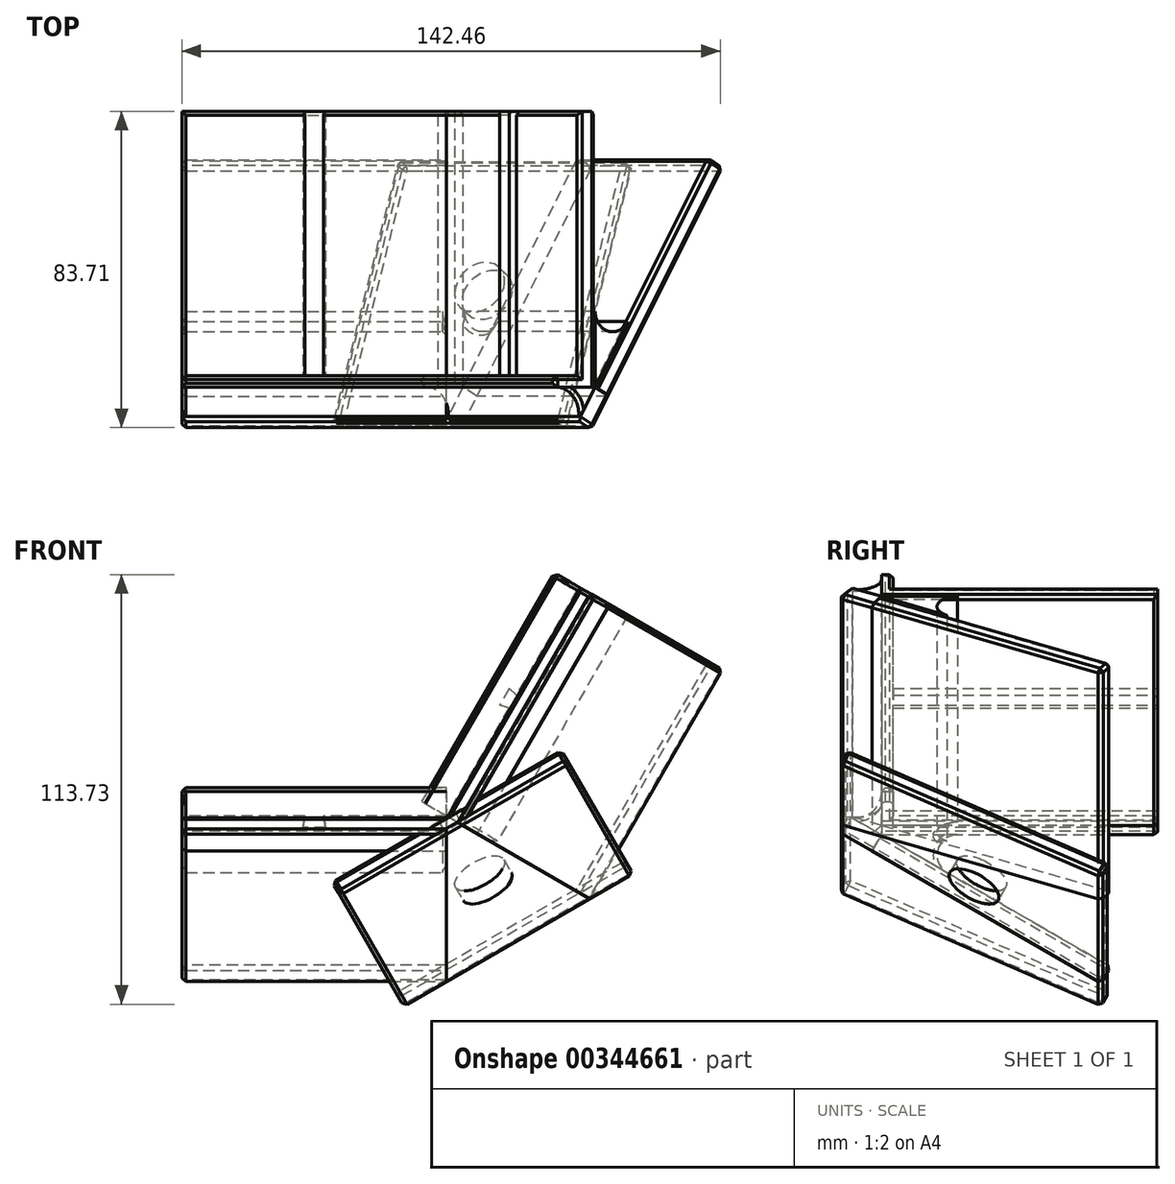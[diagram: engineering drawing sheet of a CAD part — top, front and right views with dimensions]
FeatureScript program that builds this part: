
annotation { "Feature Type Name" : "Feature", "Feature Type Description" : "" }
export const myFeature = defineFeature(function(context is Context, id is Id, definition is map)
    precondition{}
    {
        {
            var Q0;
            Q0=qCreatedBy(makeId("Top.planeOp"),FACE);
            var sketch = newSketch(context, id + "F0", { "sketchPlane" : qUnion([Q0])});
            skLineSegment(sketch, "E0.bottom", {"start": v(35, 35) * mm, "end": v(-35, 35) * mm});
            skLineSegment(sketch, "E0.top", {"start": v(35, -35) * mm, "end": v(-35, -35) * mm});
            skLineSegment(sketch, "E0.left", {"start": v(35, 35) * mm, "end": v(35, -35) * mm});
            skLineSegment(sketch, "E0.right", {"start": v(-35, 35) * mm, "end": v(-35, -35) * mm});
            skPoint(sketch, "E0.middle", {"position": v(0, 0) * mm});
            skSolve(sketch);
        }
        {
            var Q0;
            Q0=makeQuery(id+"F0.imprint","IMPRINT",FACE,{"disambiguationData":[TD([[makeQuery(id+"F0.imprint","IMPRINT",EDGE,{"derivedFrom":sQuery(id+"F0.wireOp",EDGE,"E0.bottom")}),1.0]])]});
            extrude(context, id + "F1", {"entities" : qUnion([Q0]), "depth" : 5 * mm});
        }
        {
            var Q0;
            Q0=makeQuery(id+"F1.opExtrude","SWEPT_FACE",FACE,{"disambiguationData":[OSD([sQuery(id+"F0.wireOp",EDGE,"E0.top")])]});
            var sketch = newSketch(context, id + "F2", { "sketchPlane" : qUnion([Q0])});
            skLineSegment(sketch, "E1", {"start": v(0, 5) * mm, "end": v(2.5, 5) * mm});
            skLineSegment(sketch, "E2", {"start": v(0, 2) * mm, "end": v(3, 2) * mm});
            skLineSegment(sketch, "E3", {"start": v(3, 2) * mm, "end": v(2.5, 5) * mm});
            skLineSegment(sketch, "E4", {"start": v(0, 2) * mm, "end": v(-3, 2) * mm});
            skLineSegment(sketch, "E5", {"start": v(0, 5) * mm, "end": v(-2.5, 5) * mm});
            skLineSegment(sketch, "E6", {"start": v(-2.5, 5) * mm, "end": v(-3, 2) * mm});
            skSolve(sketch);
        }
        {
            var Q0;
            Q0=makeQuery(id+"F1.opExtrude","SWEPT_FACE",FACE,{"disambiguationData":[OSD([sQuery(id+"F0.wireOp",EDGE,"E0.top")])]});
            var sketch = newSketch(context, id + "F3", { "sketchPlane" : qUnion([Q0])});
            skLineSegment(sketch, "E7.bottom", {"start": v(-35, 0) * mm, "end": v(35, 0) * mm});
            skLineSegment(sketch, "E7.top", {"start": v(-35, 12.5) * mm, "end": v(35, 12.5) * mm});
            skLineSegment(sketch, "E7.left", {"start": v(-35, 0) * mm, "end": v(-35, 12.5) * mm});
            skLineSegment(sketch, "E7.right", {"start": v(35, 0) * mm, "end": v(35, 12.5) * mm});
            skSolve(sketch);
        }
        {
            var Q0;
            Q0=qSketchRegion(id+"F3",true);
            extrude(context, id + "F4", {"entities" : qUnion([Q0]), "operationType" : NewBodyOperationType.ADD, "depth" : 3 * mm});
        }
        {
            var Q0;
            Q0=makeQuery(id+"F4.opExtrude","CAP_EDGE",EDGE,{"disambiguationData":[OSD([sQuery(id+"F3.wireOp",EDGE,"E7.bottom")])],"isStart":false});
            var Q1;
            Q1=makeQuery(id+"F4.boolean.opBoolean","MERGE",EDGE,{"derivedFrom":[makeQuery(id+"F1.opExtrude","CAP_EDGE",EDGE,{"disambiguationData":[OSD([sQuery(id+"F0.wireOp",EDGE,"E0.left")])],"isStart":true}),makeQuery(id+"F4.opExtrude","SWEPT_EDGE",EDGE,{"disambiguationData":[OSD([sQuery(id+"F3.wireOp",EDGE,"E7.bottom"),sQuery(id+"F3.wireOp",EDGE,"E7.right")])]})]});
            cPlane(context, id + "F5", {"entities" : qUnion([Q0, Q1]), "cplaneType" : CPlaneType.LINE_ANGLE, "offset" : 25 * mm, "angle" : 30 * degree, "width" : 150 * mm, "height" : 150 * mm});
        }
        {
            var Q0;
            Q0=qCreatedBy(id+"F5.planeOp",FACE);
            var sketch = newSketch(context, id + "F6", { "sketchPlane" : qUnion([Q0])});
            skLineSegment(sketch, "E8.bottom", {"start": v(-35, -32.9) * mm, "end": v(35, -32.9) * mm});
            skLineSegment(sketch, "E8.top", {"start": v(-35, 37.1) * mm, "end": v(35, 37.1) * mm});
            skLineSegment(sketch, "E8.left", {"start": v(-35, -32.9) * mm, "end": v(-35, 37.1) * mm});
            skLineSegment(sketch, "E8.right", {"start": v(35, -32.9) * mm, "end": v(35, 37.1) * mm});
            skSolve(sketch);
        }
        {
            var Q0;
            Q0=qSketchRegion(id+"F6",true);
            extrude(context, id + "F7", {"entities" : qUnion([Q0]), "operationType" : NewBodyOperationType.ADD, "oppositeDirection" : true, "depth" : 5 * mm});
        }
        {
            var Q0;
            Q0=makeQuery(id+"F7.opExtrude","SWEPT_FACE",FACE,{"disambiguationData":[OSD([sQuery(id+"F6.wireOp",EDGE,"E8.bottom")])]});
            extrude(context, id + "F8", {"entities" : qUnion([Q0]), "depth" : 10 * mm});
        }
        {
            var Q0;
            Q0=makeQuery(id+"F7.opExtrude","SWEPT_FACE",FACE,{"disambiguationData":[OSD([sQuery(id+"F6.wireOp",EDGE,"E8.right")])]});
            var sketch = newSketch(context, id + "F9", { "sketchPlane" : qUnion([Q0])});
            skLineSegment(sketch, "E9", {"start": v(-38, 0) * mm, "end": v(-20.68, -10) * mm});
            skLineSegment(sketch, "E10", {"start": v(-18, 0) * mm, "end": v(-38, 0) * mm});
            skLineSegment(sketch, "E11", {"start": v(-38, 0) * mm, "end": v(-45.8, 4.5) * mm});
            skLineSegment(sketch, "E12", {"start": v(-38, 0) * mm, "end": v(-38, 11.5) * mm});
            skArc(sketch, "E13", {"start": v(-45.8, 4.5) * mm, "mid": v(-40.34, 6.26) * mm, "end": v(-38, 11.5) * mm});
            skArc(sketch, "E14", {"start": v(-18, 0) * mm, "mid": v(-23.18, -3.97) * mm, "end": v(-20.68, -10) * mm});
            skSolve(sketch);
        }
        {
            var Q0;
            Q0=qSketchRegion(id+"F9",true);
            var Q1;
            Q1=makeQuery(id+"F7.opExtrude","SWEPT_FACE",FACE,{"disambiguationData":[OSD([sQuery(id+"F6.wireOp",EDGE,"E8.left")])]});
            extrude(context, id + "F10", {"entities" : qUnion([Q0]), "endBound" : BoundingType.UP_TO_SURFACE, "oppositeDirection" : true, "endBoundEntityFace" : qUnion([Q1]), "depth" : 25 * mm});
        }
        {
            var Q0;
            {var subQ0=sQuery(id+"F0.wireOp",EDGE,"E0.bottom");var subQ1=sQuery(id+"F0.wireOp",EDGE,"E0.top");var subQ2=sQuery(id+"F0.wireOp",EDGE,"E0.left");Q0=makeQuery(id+"F13.boolean.opBoolean","SPLIT",FACE,{"disambiguationData":[TD([makeQuery(id+"F1.opExtrude","SWEPT_FACE",FACE,{"disambiguationData":[OSD([subQ2])]})])],"derivedFrom":makeQuery(id+"F1.opExtrude","CAP_FACE",FACE,{"disambiguationData":[OSD([subQ0,subQ1,subQ2,sQuery(id+"F0.wireOp",EDGE,"E0.right")])],"isStart":false})});}
            var Q1;
            Q1=makeQuery(id+"F1.opExtrude","CAP_EDGE",EDGE,{"disambiguationData":[OSD([sQuery(id+"F0.wireOp",EDGE,"E0.left")])],"isStart":false});
            cPlane(context, id + "F11", {"entities" : qUnion([Q0, Q1]), "cplaneType" : CPlaneType.LINE_ANGLE, "offset" : 25 * mm, "angle" : 60 * degree, "oppositeDirection" : true, "width" : 150 * mm, "height" : 150 * mm});
        }
        {
            var Q0;
            Q0=makeQuery(id+"F1.opExtrude","SWEPT_BODY",BODY,{"disambiguationData":[OSD([sQuery(id+"F0.wireOp",EDGE,"E0.bottom"),sQuery(id+"F0.wireOp",EDGE,"E0.top"),sQuery(id+"F0.wireOp",EDGE,"E0.left"),sQuery(id+"F0.wireOp",EDGE,"E0.right")])]});
            var Q1;
            Q1=makeQuery(id+"F7.opExtrude","SWEPT_BODY",BODY,{"disambiguationData":[OSD([sQuery(id+"F6.wireOp",EDGE,"E8.bottom"),sQuery(id+"F6.wireOp",EDGE,"E8.top"),sQuery(id+"F6.wireOp",EDGE,"E8.left"),sQuery(id+"F6.wireOp",EDGE,"E8.right")])]});
            var Q2;
            Q2=makeQuery(id+"F8.opExtrude","SWEPT_BODY",BODY,{"disambiguationData":[OSD([sQuery(id+"F6.wireOp",EDGE,"E8.bottom")])]});
            var Q3;
            Q3=makeQuery(id+"F10.opExtrude","SWEPT_BODY",BODY,{"disambiguationData":[OSD([sQuery(id+"F9.wireOp",EDGE,"E9"),sQuery(id+"F9.wireOp",EDGE,"E10"),sQuery(id+"F9.wireOp",EDGE,"E14")])]});
            var Q4;
            Q4=makeQuery(id+"F10.opExtrude","SWEPT_BODY",BODY,{"disambiguationData":[OSD([sQuery(id+"F9.wireOp",EDGE,"E11"),sQuery(id+"F9.wireOp",EDGE,"E12"),sQuery(id+"F9.wireOp",EDGE,"E13")])]});
            var Q5;
            Q5=qCreatedBy(id+"F11.planeOp",FACE);
            mirror(context, id + "F12", {"entities" : qUnion([Q0, Q1, Q2, Q3, Q4]), "mirrorPlane" : qUnion([Q5])});
        }
        {
            var Q0;
            Q0=makeQuery(id+"F2.imprint","IMPRINT",FACE,{"disambiguationData":[TD([[makeQuery(id+"F2.imprint","IMPRINT",EDGE,{"derivedFrom":sQuery(id+"F2.wireOp",EDGE,"E1")}),1.0]])]});
            var Q1;
            Q1=makeQuery(id+"F1.opExtrude","SWEPT_FACE",FACE,{"disambiguationData":[OSD([sQuery(id+"F0.wireOp",EDGE,"E0.bottom")])]});
            extrude(context, id + "F13", {"entities" : qUnion([Q0]), "operationType" : NewBodyOperationType.REMOVE, "endBound" : BoundingType.UP_TO_SURFACE, "oppositeDirection" : true, "endBoundEntityFace" : qUnion([Q1]), "depth" : 25 * mm});
        }
        {
            var Q0;
            Q0=makeQuery(id+"F7.opExtrude","CAP_VERTEX",VERTEX,{"disambiguationData":[OSD([sQuery(id+"F6.wireOp",EDGE,"E8.top"),sQuery(id+"F6.wireOp",EDGE,"E8.right")])],"isStart":false});
            var Q1;
            Q1=makeQuery(id+"F12.opPattern","COPY",VERTEX,{"derivedFrom":makeQuery(id+"F7.opExtrude","CAP_VERTEX",VERTEX,{"disambiguationData":[OSD([sQuery(id+"F6.wireOp",EDGE,"E8.top"),sQuery(id+"F6.wireOp",EDGE,"E8.right")])],"isStart":false}),"instanceName":"1"});
            var Q2;
            Q2=makeQuery(id+"F12.opPattern","COPY",VERTEX,{"derivedFrom":makeQuery(id+"F7.opExtrude","CAP_VERTEX",VERTEX,{"disambiguationData":[OSD([sQuery(id+"F6.wireOp",EDGE,"E8.bottom"),sQuery(id+"F6.wireOp",EDGE,"E8.right")])],"isStart":false}),"instanceName":"1"});
            cPlane(context, id + "F14", {"entities" : qUnion([Q0, Q1, Q2]), "cplaneType" : CPlaneType.THREE_POINT, "offset" : 25 * mm, "width" : 150 * mm, "height" : 150 * mm});
        }
        {
            var Q0;
            Q0=qCreatedBy(id+"F14.planeOp",FACE);
            var sketch = newSketch(context, id + "F15", { "sketchPlane" : qUnion([Q0])});
            skLineSegment(sketch, "E15", {"start": v(20.57, 37.1) * mm, "end": v(63.5, 26) * mm, "construction": true});
            skLineSegment(sketch, "E16", {"start": v(20.57, -42.9) * mm, "end": v(24.76, -44) * mm, "construction": true});
            skLineSegment(sketch, "E17", {"start": v(22.67, -43.45) * mm, "end": v(42.03, 31.55) * mm, "construction": true});
            skLineSegment(sketch, "E18", {"start": v(42.03, 31.55) * mm, "end": v(8.14, 40.3) * mm});
            skLineSegment(sketch, "E19", {"start": v(42.03, 31.55) * mm, "end": v(75.92, 22.8) * mm});
            skLineSegment(sketch, "E20", {"start": v(22.67, -43.45) * mm, "end": v(-11.22, -34.7) * mm});
            skLineSegment(sketch, "E21", {"start": v(22.67, -43.45) * mm, "end": v(56.56, -52.2) * mm});
            skLineSegment(sketch, "E22", {"start": v(56.56, -52.2) * mm, "end": v(75.92, 22.8) * mm});
            skLineSegment(sketch, "E23", {"start": v(8.14, 40.3) * mm, "end": v(-11.22, -34.7) * mm});
            skSolve(sketch);
        }
        {
            var Q0;
            Q0=makeQuery(id+"F15.imprint","IMPRINT",FACE,{"disambiguationData":[TD([[makeQuery(id+"F15.imprint","IMPRINT",EDGE,{"derivedFrom":sQuery(id+"F15.wireOp",EDGE,"E18")}),1.0]])]});
            var Q1;
            Q1=makeQuery(id+"F10.opExtrude","CAP_VERTEX",VERTEX,{"disambiguationData":[OSD([sQuery(id+"F6.wireOp",EDGE,"E8.right"),sQuery(id+"F9.wireOp",EDGE,"E9"),sQuery(id+"F9.wireOp",EDGE,"E14")])],"isStart":true});
            extrude(context, id + "F16", {"entities" : qUnion([Q0]), "endBound" : BoundingType.UP_TO_VERTEX, "endBoundEntityVertex" : qUnion([Q1]), "depth" : 25 * mm});
        }
        {
            var Q0;
            Q0=makeQuery(id+"F4.boolean.opBoolean","MERGE",EDGE,{"derivedFrom":[makeQuery(id+"F1.opExtrude","CAP_EDGE",EDGE,{"disambiguationData":[OSD([sQuery(id+"F0.wireOp",EDGE,"E0.left")])],"isStart":true}),makeQuery(id+"F4.opExtrude","SWEPT_EDGE",EDGE,{"disambiguationData":[OSD([sQuery(id+"F3.wireOp",EDGE,"E7.bottom"),sQuery(id+"F3.wireOp",EDGE,"E7.right")])]})]});
            cPoint(context, id + "F17", {"entities" : qUnion([Q0]), "parameter" : 0.5});
        }
        {
            var Q0;
            Q0=makeQuery(id+"F1.opExtrude","CAP_VERTEX",VERTEX,{"disambiguationData":[OSD([sQuery(id+"F0.wireOp",EDGE,"E0.bottom"),sQuery(id+"F0.wireOp",EDGE,"E0.left")])],"isStart":true});
            var Q1;
            Q1 = qCreatedBy(id + "F17" ,VERTEX);
            var Q2;
            Q2=makeQuery(id+"F12.opPattern","COPY",VERTEX,{"derivedFrom":makeQuery(id+"F1.opExtrude","CAP_VERTEX",VERTEX,{"disambiguationData":[OSD([sQuery(id+"F0.wireOp",EDGE,"E0.bottom"),sQuery(id+"F0.wireOp",EDGE,"E0.left")])],"isStart":true}),"instanceName":"1"});
            cPlane(context, id + "F18", {"entities" : qUnion([Q0, Q1, Q2]), "cplaneType" : CPlaneType.THREE_POINT, "offset" : 25 * mm, "width" : 150 * mm, "height" : 150 * mm});
        }
        {
            var Q0;
            Q0=qCreatedBy(id+"F18.planeOp",FACE);
            var sketch = newSketch(context, id + "F19", { "sketchPlane" : qUnion([Q0])});
            skLineSegment(sketch, "E24", {"start": v(35.31, -35) * mm, "end": v(35.31, 38) * mm});
            skLineSegment(sketch, "E25", {"start": v(35.31, 38) * mm, "end": v(30.31, 38) * mm});
            skLineSegment(sketch, "E26", {"start": v(30.31, 38) * mm, "end": v(30.31, -35) * mm});
            skLineSegment(sketch, "E27", {"start": v(30.31, -35) * mm, "end": v(35.31, -35) * mm});
            skSolve(sketch);
        }
        {
            var Q0;
            Q0 = qSketchRegion(id + "F19", true);
            var Q1;
            Q1=makeQuery(id+"F1.opExtrude","CAP_VERTEX",VERTEX,{"disambiguationData":[OSD([sQuery(id+"F0.wireOp",EDGE,"E0.top"),sQuery(id+"F0.wireOp",EDGE,"E0.left")])],"isStart":false});
            extrude(context, id + "F20", {"entities" : qUnion([Q0]), "endBound" : BoundingType.UP_TO_VERTEX, "oppositeDirection" : true, "endBoundEntityVertex" : qUnion([Q1]), "depth" : 25 * mm});
        }
        {
            var Q0;
            Q0=makeQuery(id+"F12.opPattern","COPY",FACE,{"derivedFrom":makeQuery(id+"F1.opExtrude","SWEPT_FACE",FACE,{"disambiguationData":[OSD([sQuery(id+"F0.wireOp",EDGE,"E0.bottom")])]}),"instanceName":"1"});
            var sketch = newSketch(context, id + "F21", { "sketchPlane" : qUnion([Q0])});
            skLineSegment(sketch, "E28", {"start": v(-53.5, 37.04) * mm, "end": v(-51.5, 33.58) * mm});
            skPoint(sketch, "E28.endSnap0", {"position": v(-57.27, 33.58) * mm});
            skLineSegment(sketch, "E29", {"start": v(-50.33, 36.56) * mm, "end": v(-49.08, 34.4) * mm});
            skLineSegment(sketch, "E30", {"start": v(-50.33, 36.56) * mm, "end": v(-51.58, 38.73) * mm});
            skLineSegment(sketch, "E31", {"start": v(-53.5, 37.04) * mm, "end": v(-51.58, 38.73) * mm});
            skLineSegment(sketch, "E32", {"start": v(-51.5, 33.58) * mm, "end": v(-49.08, 34.4) * mm});
            skSolve(sketch);
        }
        {
            var Q0;
            Q0 = qSketchRegion(id + "F21", true);
            var Q1;
            Q1=makeQuery(id+"F12.opPattern","COPY",FACE,{"derivedFrom":makeQuery(id+"F4.opExtrude","CAP_FACE",FACE,{"disambiguationData":[OSD([sQuery(id+"F3.wireOp",EDGE,"E7.bottom"),sQuery(id+"F3.wireOp",EDGE,"E7.top"),sQuery(id+"F3.wireOp",EDGE,"E7.left"),sQuery(id+"F3.wireOp",EDGE,"E7.right")])],"isStart":true}),"instanceName":"1"});
            extrude(context, id + "F22", {"entities" : qUnion([Q0]), "operationType" : NewBodyOperationType.ADD, "endBound" : BoundingType.UP_TO_SURFACE, "oppositeDirection" : true, "endBoundEntityFace" : qUnion([Q1]), "depth" : 25 * mm});
        }
        {
            var Q0;
            Q0=makeQuery(id+"F16.opExtrude","CAP_FACE",FACE,{"disambiguationData":[OSD([sQuery(id+"F15.wireOp",EDGE,"E18"),sQuery(id+"F15.wireOp",EDGE,"E19"),sQuery(id+"F15.wireOp",EDGE,"E20"),sQuery(id+"F15.wireOp",EDGE,"E21"),sQuery(id+"F15.wireOp",EDGE,"E22"),sQuery(id+"F15.wireOp",EDGE,"E23")])],"isStart":true});
            var sketch = newSketch(context, id + "F23", { "sketchPlane" : qUnion([Q0])});
            skLineSegment(sketch, "E33", {"start": v(66.24, 14.7) * mm, "end": v(-1.02, -4.82) * mm, "construction": true});
            skLineSegment(sketch, "E34", {"start": v(42.03, -31.55) * mm, "end": v(22.67, 43.45) * mm, "construction": true});
            skCircle(sketch, "E35", {"center": v(32.61, 4.94) * mm, "radius": 7.38 * mm});
            skSolve(sketch);
        }
        {
            var Q0;
            Q0=makeQuery(id+"F23.imprint","IMPRINT",FACE,{"disambiguationData":[TD([[makeQuery(id+"F23.imprint","IMPRINT",EDGE,{"derivedFrom":sQuery(id+"F23.wireOp",EDGE,"E35")}),1.0]])]});
            var Q1;
            Q1=makeQuery(id+"F16.opExtrude","CAP_FACE",FACE,{"disambiguationData":[OSD([sQuery(id+"F15.wireOp",EDGE,"E18"),sQuery(id+"F15.wireOp",EDGE,"E19"),sQuery(id+"F15.wireOp",EDGE,"E20"),sQuery(id+"F15.wireOp",EDGE,"E21"),sQuery(id+"F15.wireOp",EDGE,"E22"),sQuery(id+"F15.wireOp",EDGE,"E23")])],"isStart":false});
            extrude(context, id + "F24", {"entities" : qUnion([Q0]), "operationType" : NewBodyOperationType.REMOVE, "endBound" : BoundingType.UP_TO_SURFACE, "oppositeDirection" : true, "endBoundEntityFace" : qUnion([Q1]), "depth" : 25 * mm});
        }
        {
            var Q0;
            Q0=makeQuery(id+"F1.opExtrude","CAP_EDGE",EDGE,{"disambiguationData":[OSD([sQuery(id+"F0.wireOp",EDGE,"E0.right")])],"isStart":false});
            var Q1;
            {var subQ0=sQuery(id+"F0.wireOp",EDGE,"E0.right");var subQ1=sQuery(id+"F0.wireOp",EDGE,"E0.bottom");Q1=makeQuery(id+"F13.boolean.opBoolean","SPLIT",EDGE,{"disambiguationData":[TD([makeQuery(id+"F1.opExtrude","SWEPT_FACE",FACE,{"disambiguationData":[OSD([subQ0])]})])],"derivedFrom":makeQuery(id+"F1.opExtrude","CAP_EDGE",EDGE,{"disambiguationData":[OSD([subQ1])],"isStart":false})});}
            var Q2;
            {var subQ0=sQuery(id+"F0.wireOp",EDGE,"E0.left");var subQ1=sQuery(id+"F0.wireOp",EDGE,"E0.bottom");Q2=makeQuery(id+"F13.boolean.opBoolean","SPLIT",EDGE,{"disambiguationData":[TD([makeQuery(id+"F1.opExtrude","SWEPT_FACE",FACE,{"disambiguationData":[OSD([subQ0])]})])],"derivedFrom":makeQuery(id+"F1.opExtrude","CAP_EDGE",EDGE,{"disambiguationData":[OSD([subQ1])],"isStart":false})});}
            var Q3;
            Q3=makeQuery(id+"F12.opPattern","COPY",EDGE,{"derivedFrom":makeQuery(id+"F1.opExtrude","CAP_EDGE",EDGE,{"disambiguationData":[OSD([sQuery(id+"F0.wireOp",EDGE,"E0.bottom")])],"isStart":false}),"instanceName":"1"});
            var Q4;
            Q4=makeQuery(id+"F4.opExtrude","CAP_EDGE",EDGE,{"disambiguationData":[OSD([sQuery(id+"F3.wireOp",EDGE,"E7.left")])],"isStart":true});
            var Q5;
            Q5=makeQuery(id+"F4.opExtrude","CAP_EDGE",EDGE,{"disambiguationData":[OSD([sQuery(id+"F3.wireOp",EDGE,"E7.top")])],"isStart":true});
            var Q6;
            Q6=makeQuery(id+"F4.opExtrude","SWEPT_EDGE",EDGE,{"disambiguationData":[OSD([sQuery(id+"F3.wireOp",EDGE,"E7.top"),sQuery(id+"F3.wireOp",EDGE,"E7.left")])]});
            var Q7;
            Q7=makeQuery(id+"F4.opExtrude","CAP_EDGE",EDGE,{"disambiguationData":[OSD([sQuery(id+"F3.wireOp",EDGE,"E7.top")])],"isStart":false});
            var Q8;
            Q8=makeQuery(id+"F12.opPattern","COPY",EDGE,{"derivedFrom":makeQuery(id+"F4.opExtrude","CAP_EDGE",EDGE,{"disambiguationData":[OSD([sQuery(id+"F3.wireOp",EDGE,"E7.top")])],"isStart":true}),"instanceName":"1"});
            var Q9;
            Q9=makeQuery(id+"F12.opPattern","COPY",EDGE,{"derivedFrom":makeQuery(id+"F4.opExtrude","CAP_EDGE",EDGE,{"disambiguationData":[OSD([sQuery(id+"F3.wireOp",EDGE,"E7.top")])],"isStart":false}),"instanceName":"1"});
            var Q10;
            Q10=makeQuery(id+"F12.opPattern","COPY",EDGE,{"derivedFrom":makeQuery(id+"F4.opExtrude","SWEPT_EDGE",EDGE,{"disambiguationData":[OSD([sQuery(id+"F3.wireOp",EDGE,"E7.top"),sQuery(id+"F3.wireOp",EDGE,"E7.left")])]}),"instanceName":"1"});
            var Q11;
            Q11=makeQuery(id+"F12.opPattern","COPY",EDGE,{"derivedFrom":makeQuery(id+"F4.opExtrude","CAP_EDGE",EDGE,{"disambiguationData":[OSD([sQuery(id+"F3.wireOp",EDGE,"E7.left")])],"isStart":true}),"instanceName":"1"});
            var Q12;
            Q12=makeQuery(id+"F12.opPattern","COPY",EDGE,{"derivedFrom":makeQuery(id+"F1.opExtrude","CAP_EDGE",EDGE,{"disambiguationData":[OSD([sQuery(id+"F0.wireOp",EDGE,"E0.right")])],"isStart":false}),"instanceName":"1"});
            var Q13;
            Q13=makeQuery(id+"F12.opPattern","COPY",EDGE,{"derivedFrom":makeQuery(id+"F4.boolean.opBoolean","MERGE",EDGE,{"derivedFrom":[makeQuery(id+"F1.opExtrude","CAP_EDGE",EDGE,{"disambiguationData":[OSD([sQuery(id+"F0.wireOp",EDGE,"E0.right")])],"isStart":true}),makeQuery(id+"F4.opExtrude","SWEPT_EDGE",EDGE,{"disambiguationData":[OSD([sQuery(id+"F3.wireOp",EDGE,"E7.bottom"),sQuery(id+"F3.wireOp",EDGE,"E7.left")])]})]}),"instanceName":"1"});
            var Q14;
            Q14=makeQuery(id+"F12.opPattern","COPY",EDGE,{"derivedFrom":makeQuery(id+"F7.opExtrude","CAP_EDGE",EDGE,{"disambiguationData":[OSD([sQuery(id+"F6.wireOp",EDGE,"E8.left")])],"isStart":true}),"instanceName":"1"});
            var Q15;
            Q15=makeQuery(id+"F12.opPattern","COPY",EDGE,{"derivedFrom":makeQuery(id+"F7.opExtrude","CAP_EDGE",EDGE,{"disambiguationData":[OSD([sQuery(id+"F6.wireOp",EDGE,"E8.left")])],"isStart":false}),"instanceName":"1"});
            var Q16;
            {var subQ0=sQuery(id+"F6.wireOp",EDGE,"E8.left");var subQ1=sQuery(id+"F6.wireOp",EDGE,"E8.bottom");Q16=makeQuery(id+"F12.opPattern","COPY",EDGE,{"derivedFrom":makeQuery(id+"F8.opExtrude","SWEPT_EDGE",EDGE,{"disambiguationData":[OSD([subQ1,subQ0]),TDD([makeQuery(id+"F7.opExtrude","CAP_VERTEX",VERTEX,{"disambiguationData":[OSD([subQ1,subQ0])],"isStart":false})])]}),"instanceName":"1"});}
            var Q17;
            Q17=makeQuery(id+"F12.opPattern","COPY",EDGE,{"derivedFrom":makeQuery(id+"F8.opExtrude","CAP_EDGE",EDGE,{"disambiguationData":[OSD([sQuery(id+"F6.wireOp",EDGE,"E8.bottom"),sQuery(id+"F6.wireOp",EDGE,"E8.left")])],"isStart":false}),"instanceName":"1"});
            var Q18;
            Q18=makeQuery(id+"F12.opPattern","COPY",EDGE,{"derivedFrom":makeQuery(id+"F10.opExtrude","CAP_EDGE",EDGE,{"disambiguationData":[OSD([sQuery(id+"F9.wireOp",EDGE,"E13")])],"isStart":false}),"instanceName":"1"});
            var Q19;
            {var subQ0=sQuery(id+"F6.wireOp",EDGE,"E8.bottom");Q19=makeQuery(id+"F12.opPattern","COPY",EDGE,{"derivedFrom":makeQuery(id+"F8.opExtrude","CAP_EDGE",EDGE,{"disambiguationData":[OSD([subQ0]),TDD([makeQuery(id+"F7.opExtrude","CAP_EDGE",EDGE,{"disambiguationData":[OSD([subQ0])],"isStart":true})])],"isStart":false}),"instanceName":"1"});}
            var Q20;
            {var subQ0=sQuery(id+"F6.wireOp",EDGE,"E8.bottom");Q20=makeQuery(id+"F12.opPattern","COPY",EDGE,{"derivedFrom":makeQuery(id+"F8.opExtrude","CAP_EDGE",EDGE,{"disambiguationData":[OSD([subQ0]),TDD([makeQuery(id+"F7.opExtrude","CAP_EDGE",EDGE,{"disambiguationData":[OSD([subQ0])],"isStart":false})])],"isStart":false}),"instanceName":"1"});}
            var Q21;
            {var subQ0=sQuery(id+"F6.wireOp",EDGE,"E8.bottom");Q21=makeQuery(id+"F8.opExtrude","CAP_EDGE",EDGE,{"disambiguationData":[OSD([subQ0]),TDD([makeQuery(id+"F7.opExtrude","CAP_EDGE",EDGE,{"disambiguationData":[OSD([subQ0])],"isStart":true})])],"isStart":false});}
            var Q22;
            {var subQ0=sQuery(id+"F6.wireOp",EDGE,"E8.bottom");Q22=makeQuery(id+"F8.opExtrude","CAP_EDGE",EDGE,{"disambiguationData":[OSD([subQ0]),TDD([makeQuery(id+"F7.opExtrude","CAP_EDGE",EDGE,{"disambiguationData":[OSD([subQ0])],"isStart":false})])],"isStart":false});}
            var Q23;
            Q23=makeQuery(id+"F8.opExtrude","CAP_EDGE",EDGE,{"disambiguationData":[OSD([sQuery(id+"F6.wireOp",EDGE,"E8.bottom"),sQuery(id+"F6.wireOp",EDGE,"E8.left")])],"isStart":false});
            var Q24;
            Q24=makeQuery(id+"F10.opExtrude","CAP_EDGE",EDGE,{"disambiguationData":[OSD([sQuery(id+"F9.wireOp",EDGE,"E14")])],"isStart":false});
            var Q25;
            Q25=makeQuery(id+"F4.boolean.opBoolean","MERGE",EDGE,{"derivedFrom":[makeQuery(id+"F1.opExtrude","CAP_EDGE",EDGE,{"disambiguationData":[OSD([sQuery(id+"F0.wireOp",EDGE,"E0.right")])],"isStart":true}),makeQuery(id+"F4.opExtrude","SWEPT_EDGE",EDGE,{"disambiguationData":[OSD([sQuery(id+"F3.wireOp",EDGE,"E7.bottom"),sQuery(id+"F3.wireOp",EDGE,"E7.left")])]})]});
            var Q26;
            Q26=makeQuery(id+"F10.opExtrude","CAP_EDGE",EDGE,{"disambiguationData":[OSD([sQuery(id+"F9.wireOp",EDGE,"E13")])],"isStart":false});
            var Q27;
            Q27=makeQuery(id+"F7.opExtrude","CAP_EDGE",EDGE,{"disambiguationData":[OSD([sQuery(id+"F6.wireOp",EDGE,"E8.left")])],"isStart":false});
            var Q28;
            {var subQ0=sQuery(id+"F6.wireOp",EDGE,"E8.left");var subQ1=sQuery(id+"F6.wireOp",EDGE,"E8.bottom");Q28=makeQuery(id+"F8.opExtrude","SWEPT_EDGE",EDGE,{"disambiguationData":[OSD([subQ1,subQ0]),TDD([makeQuery(id+"F7.opExtrude","CAP_VERTEX",VERTEX,{"disambiguationData":[OSD([subQ1,subQ0])],"isStart":false})])]});}
            var Q29;
            Q29=makeQuery(id+"F7.opExtrude","SWEPT_EDGE",EDGE,{"disambiguationData":[OSD([sQuery(id+"F6.wireOp",EDGE,"E8.top"),sQuery(id+"F6.wireOp",EDGE,"E8.left")])]});
            var Q30;
            Q30=makeQuery(id+"F7.opExtrude","CAP_EDGE",EDGE,{"disambiguationData":[OSD([sQuery(id+"F6.wireOp",EDGE,"E8.left")])],"isStart":true});
            var Q31;
            Q31=makeQuery(id+"F7.opExtrude","CAP_EDGE",EDGE,{"disambiguationData":[OSD([sQuery(id+"F6.wireOp",EDGE,"E8.top")])],"isStart":false});
            var Q32;
            Q32=makeQuery(id+"F7.opExtrude","CAP_EDGE",EDGE,{"disambiguationData":[OSD([sQuery(id+"F6.wireOp",EDGE,"E8.top")])],"isStart":true});
            var Q33;
            Q33=makeQuery(id+"F12.opPattern","COPY",EDGE,{"derivedFrom":makeQuery(id+"F7.opExtrude","CAP_EDGE",EDGE,{"disambiguationData":[OSD([sQuery(id+"F6.wireOp",EDGE,"E8.top")])],"isStart":true}),"instanceName":"1"});
            var Q34;
            Q34=makeQuery(id+"F12.opPattern","COPY",EDGE,{"derivedFrom":makeQuery(id+"F7.opExtrude","CAP_EDGE",EDGE,{"disambiguationData":[OSD([sQuery(id+"F6.wireOp",EDGE,"E8.top")])],"isStart":false}),"instanceName":"1"});
            var Q35;
            Q35=makeQuery(id+"F12.opPattern","COPY",EDGE,{"derivedFrom":makeQuery(id+"F7.opExtrude","SWEPT_EDGE",EDGE,{"disambiguationData":[OSD([sQuery(id+"F6.wireOp",EDGE,"E8.top"),sQuery(id+"F6.wireOp",EDGE,"E8.left")])]}),"instanceName":"1"});
            var Q36;
            Q36=makeQuery(id+"F1.opExtrude","CAP_EDGE",EDGE,{"disambiguationData":[OSD([sQuery(id+"F0.wireOp",EDGE,"E0.bottom")])],"isStart":true});
            var Q37;
            Q37=makeQuery(id+"F20.opExtrude","CAP_EDGE",EDGE,{"disambiguationData":[OSD([sQuery(id+"F19.wireOp",EDGE,"E27")])],"isStart":true});
            var Q38;
            Q38=makeQuery(id+"F12.opPattern","COPY",EDGE,{"derivedFrom":makeQuery(id+"F1.opExtrude","CAP_EDGE",EDGE,{"disambiguationData":[OSD([sQuery(id+"F0.wireOp",EDGE,"E0.bottom")])],"isStart":true}),"instanceName":"1"});
            var Q39;
            Q39=makeQuery(id+"F12.opPattern","COPY",EDGE,{"derivedFrom":makeQuery(id+"F10.opExtrude","CAP_EDGE",EDGE,{"disambiguationData":[OSD([sQuery(id+"F9.wireOp",EDGE,"E14")])],"isStart":true}),"instanceName":"1"});
            var Q40;
            Q40=makeQuery(id+"F10.opExtrude","CAP_EDGE",EDGE,{"disambiguationData":[OSD([sQuery(id+"F9.wireOp",EDGE,"E14")])],"isStart":true});
            var Q41;
            Q41=makeQuery(id+"F16.opExtrude","SWEPT_FACE",FACE,{"disambiguationData":[OSD([sQuery(id+"F15.wireOp",EDGE,"E23")])]});
            var Q42;
            Q42=makeQuery(id+"F16.opExtrude","SWEPT_FACE",FACE,{"disambiguationData":[OSD([sQuery(id+"F15.wireOp",EDGE,"E20"),sQuery(id+"F15.wireOp",EDGE,"E21")])]});
            var Q43;
            Q43=makeQuery(id+"F16.opExtrude","SWEPT_FACE",FACE,{"disambiguationData":[OSD([sQuery(id+"F15.wireOp",EDGE,"E22")])]});
            var Q44;
            Q44=makeQuery(id+"F16.opExtrude","SWEPT_FACE",FACE,{"disambiguationData":[OSD([sQuery(id+"F15.wireOp",EDGE,"E18"),sQuery(id+"F15.wireOp",EDGE,"E19")])]});
            chamfer(context, id + "F25", {"entities" : qUnion([Q0, Q1, Q2, Q3, Q4, Q5, Q6, Q7, Q8, Q9, Q10, Q11, Q12, Q13, Q14, Q15, Q16, Q17, Q18, Q19, Q20, Q21, Q22, Q23, Q24, Q25, Q26, Q27, Q28, Q29, Q30, Q31, Q32, Q33, Q34, Q35, Q36, Q37, Q38, Q39, Q40, Q41, Q42, Q43, Q44]), "width" : 1 * mm});
        }
    });
